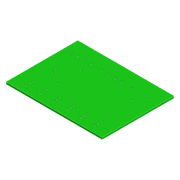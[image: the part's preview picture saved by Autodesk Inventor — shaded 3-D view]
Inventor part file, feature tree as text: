
AUTODESK INVENTOR PART (.ipt)
format: ipt  version: 2022 (Build 260153000, 153)  size: 196,096 bytes
history: native  units: mm
features: extrude x5, sketch x5
ambient origin geometry x8: Origin, YZ Plane, XZ Plane, XY Plane, X Axis, Y Axis, Z Axis, Center Point
bodies: Solid1 (feature_tree)
feature tree (10):
  extrude  "Extrusion1"  Depth=56.0mm
  extrude  "Extrusion2"  Depth=1.524mm
  extrude  "Extrusion3"  Depth=10.0mm
  extrude  "Extrusion4"  Depth=1.02mm
  extrude  "Extrusion5"  Depth=10.0mm TaperAngle=0.0deg
  sketch  "Sketch1"  dims[d0=75.0mm d1=56.0mm]
  sketch  "Sketch2"  dims[d2=1.524mm d3=0.0mm d6=10.714286mm]
  sketch  "Sketch3"  dims[d7=5.0mm d8=60.0mm d10=10.714286mm d11=10.0mm d13=10.0mm]
  sketch  "Sketch4"  dims[d15=0.0mm d16=0.0mm d17=1.02mm d18=1.02mm d19=1.02mm d20=1.02mm]
  sketch  "Sketch5"  dims[d21=10.0mm d22=0.0mm d24=10.0mm d25=0.0mm d26=11.0mm d27=5.26mm d28=1.02mm d29=1.02mm d30=1.02mm d31=1.02mm d32=1.02mm d33=1.02mm d34=1.02mm d35=1.02mm d36=1.02mm d37=1.02mm d38=1.02mm d39=1.02mm d40=0.0mm d41=0.0mm]
